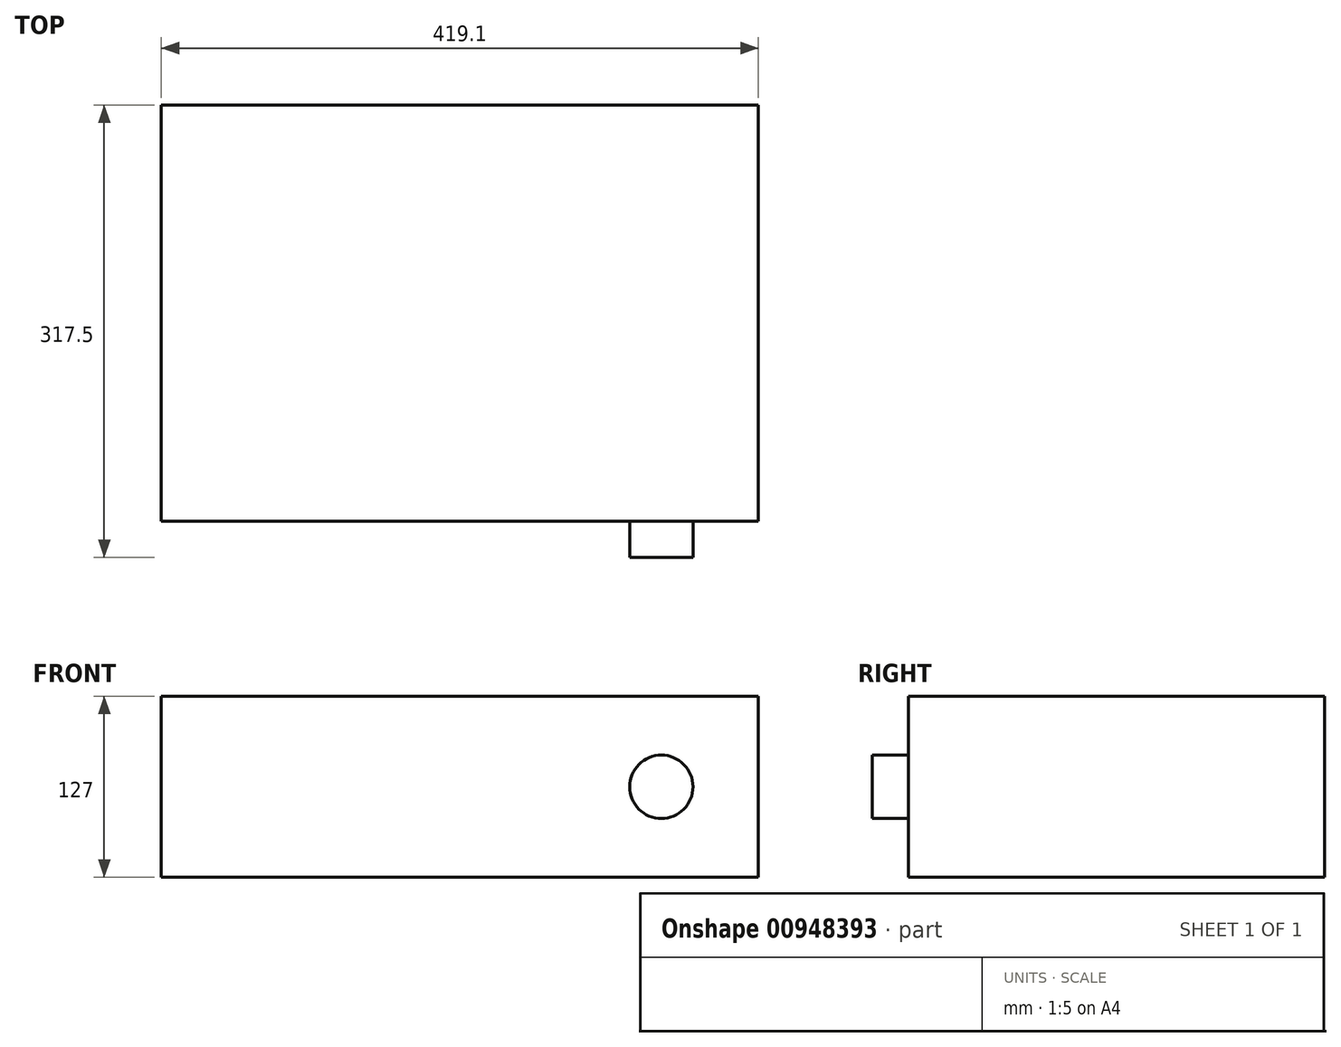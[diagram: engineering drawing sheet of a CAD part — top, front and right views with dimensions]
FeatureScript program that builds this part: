
annotation { "Feature Type Name" : "Feature", "Feature Type Description" : "" }
export const myFeature = defineFeature(function(context is Context, id is Id, definition is map)
    precondition{}
    {
        {
            var Q0;
            Q0=qCreatedBy(makeId("Top.planeOp"),FACE);
            var sketch = newSketch(context, id + "F0", { "sketchPlane" : qUnion([Q0])});
            skLineSegment(sketch, "E0.bottom", {"start": v(209.55, 146.05) * mm, "end": v(-209.55, 146.05) * mm});
            skLineSegment(sketch, "E0.top", {"start": v(209.55, -146.05) * mm, "end": v(-209.55, -146.05) * mm});
            skLineSegment(sketch, "E0.left", {"start": v(209.55, 146.05) * mm, "end": v(209.55, -146.05) * mm});
            skLineSegment(sketch, "E0.right", {"start": v(-209.55, 146.05) * mm, "end": v(-209.55, -146.05) * mm});
            skPoint(sketch, "E0.middle", {"position": v(0, 0) * mm});
            skSolve(sketch);
        }
        {
            var Q0;
            Q0=makeQuery(id+"F0.imprint","IMPRINT",FACE,{"disambiguationData":[TD([[makeQuery(id+"F0.imprint","IMPRINT",EDGE,{"derivedFrom":sQuery(id+"F0.wireOp",EDGE,"E0.bottom")}),1.0]])]});
            extrude(context, id + "F1", {"entities" : qUnion([Q0]), "depth" : 127 * mm, "offsetDistance" : 25.4 * mm});
        }
        {
            var Q0;
            Q0=makeQuery(id+"F1.opExtrude","SWEPT_FACE",FACE,{"disambiguationData":[OSD([sQuery(id+"F0.wireOp",EDGE,"E0.top")])]});
            var sketch = newSketch(context, id + "F2", { "sketchPlane" : qUnion([Q0])});
            skCircle(sketch, "E1", {"center": v(141.43, 63.5) * mm, "radius": 22.23 * mm});
            skPoint(sketch, "E1.centerSnap0", {"position": v(209.55, 63.5) * mm});
            skSolve(sketch);
        }
        {
            var Q0;
            Q0=makeQuery(id+"F2.imprint","IMPRINT",FACE,{"disambiguationData":[TD([[makeQuery(id+"F2.imprint","IMPRINT",EDGE,{"derivedFrom":sQuery(id+"F2.wireOp",EDGE,"E1")}),1.0]])]});
            extrude(context, id + "F3", {"entities" : qUnion([Q0]), "operationType" : NewBodyOperationType.ADD, "depth" : 25.4 * mm, "offsetDistance" : 25.4 * mm});
        }
    });
